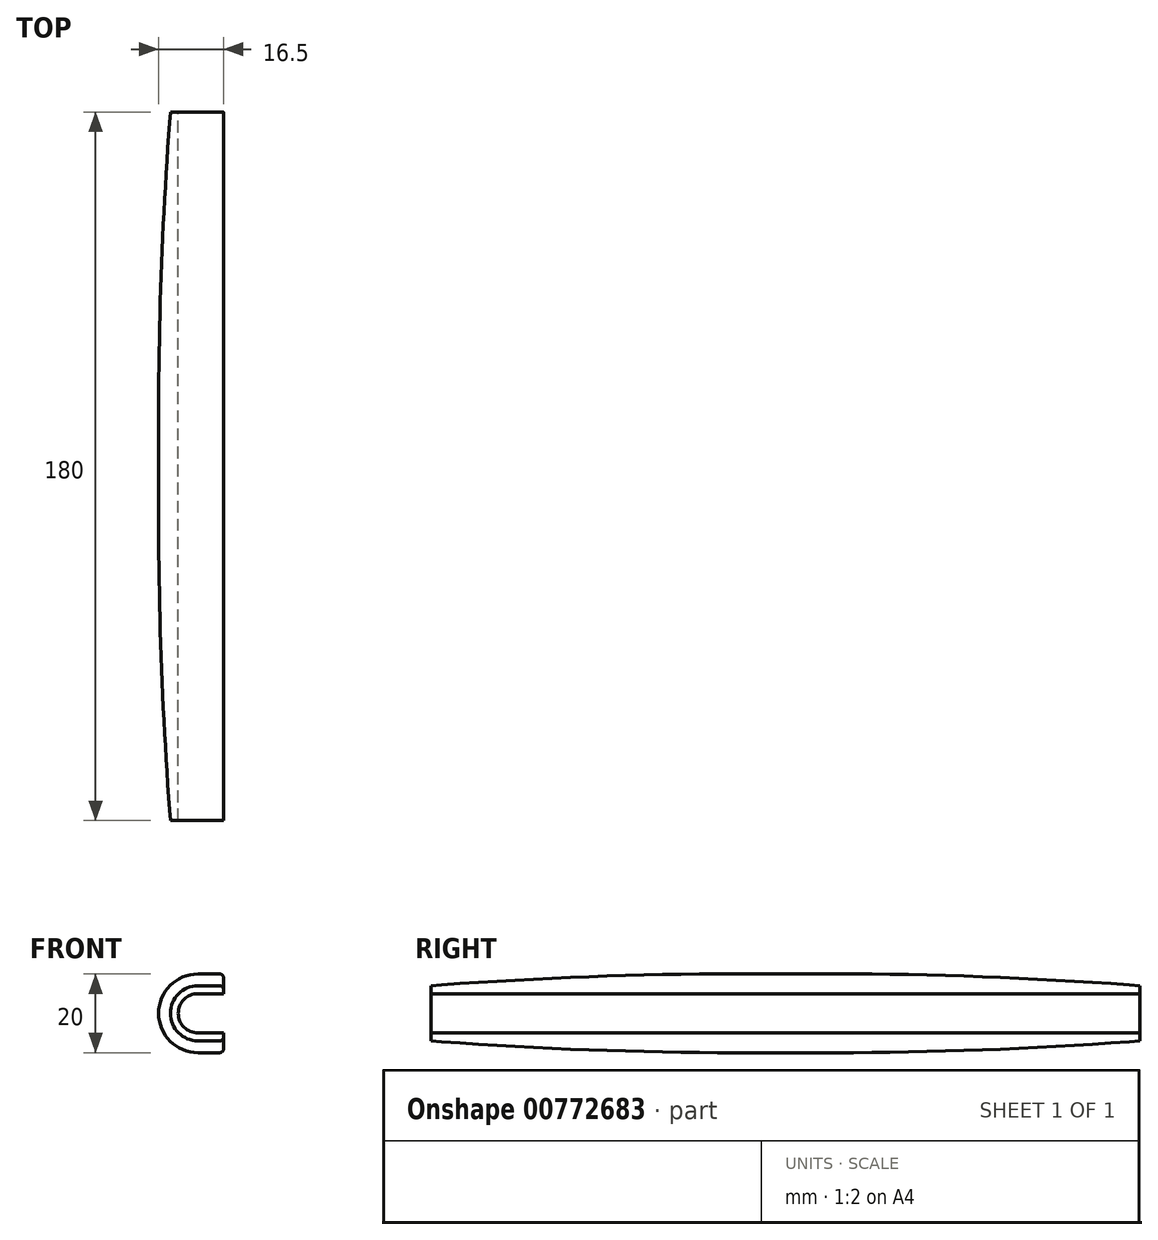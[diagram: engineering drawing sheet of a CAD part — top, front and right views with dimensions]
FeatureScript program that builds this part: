
annotation { "Feature Type Name" : "Feature", "Feature Type Description" : "" }
export const myFeature = defineFeature(function(context is Context, id is Id, definition is map)
    precondition{}
    {
        {
            var Q0;
            Q0=qCreatedBy(makeId("Front.planeOp"),FACE);
            var sketch = newSketch(context, id + "F0", { "sketchPlane" : qUnion([Q0])});
            skLineSegment(sketch, "E0.bottom", {"start": v(6.5, 5) * mm, "end": v(-6.5, 5) * mm});
            skLineSegment(sketch, "E0.top", {"start": v(6.5, -5) * mm, "end": v(-6.5, -5) * mm});
            skLineSegment(sketch, "E0.left", {"start": v(6.5, 5) * mm, "end": v(6.5, -5) * mm, "construction": true});
            skLineSegment(sketch, "E0.right", {"start": v(-6.5, 5) * mm, "end": v(-6.5, -5) * mm, "construction": true});
            skPoint(sketch, "E0.middle", {"position": v(0, 0) * mm});
            skCircle(sketch, "E1", {"center": v(-6.5, 0) * mm, "radius": 5 * mm});
            skLineSegment(sketch, "E2", {"start": v(0, 0) * mm, "end": v(0, 14.83) * mm, "construction": true});
            skCircle(sketch, "E3.MirrorC", {"center": v(6.5, 0) * mm, "radius": 5 * mm});
            skPoint(sketch, "E4", {"position": v(-11.5, 0) * mm});
            skPoint(sketch, "E5", {"position": v(11.5, 0) * mm});
            skArc(sketch, "E6", {"start": v(-6.5, 10) * mm, "mid": v(-16.5, 0) * mm, "end": v(-6.5, -10) * mm});
            skPoint(sketch, "E7", {"position": v(-16.5, 0) * mm});
            skLineSegment(sketch, "E8", {"start": v(-6.5, 10) * mm, "end": v(0, 10) * mm});
            skLineSegment(sketch, "E9", {"start": v(0, 0) * mm, "end": v(-6.5, 0) * mm, "construction": true});
            skLineSegment(sketch, "E10.MirrorCS", {"start": v(-6.5, -10) * mm, "end": v(0, -10) * mm});
            skLineSegment(sketch, "E11.MirrorCS", {"start": v(6.5, -10) * mm, "end": v(0, -10) * mm});
            skArc(sketch, "E12.MirrorC", {"start": v(-2.16, -5) * mm, "mid": v(-3.5, 0) * mm, "end": v(-2.16, 5) * mm});
            skLineSegment(sketch, "E13.MirrorCS", {"start": v(6.5, 10) * mm, "end": v(0, 10) * mm});
            skLineSegment(sketch, "E14", {"start": v(0, 10) * mm, "end": v(0, -10) * mm});
            skArc(sketch, "E15.trimOffspring", {"start": v(0, 7.6) * mm, "mid": v(16.5, 0) * mm, "end": v(0, -7.6) * mm});
            skArc(sketch, "E16.trimOffspring", {"start": v(0, -7.6) * mm, "mid": v(3.5, 0) * mm, "end": v(0, 7.6) * mm});
            skSolve(sketch);
        }
        {
            var Q0;
            Q0=makeQuery(id+"F0.imprint","IMPRINT",FACE,{"disambiguationData":[TD([[makeQuery(id+"F0.imprint","IMPRINT",EDGE,{"derivedFrom":sQuery(id+"F0.wireOp",EDGE,"E6")}),1.0]])]});
            extrude(context, id + "F1", {"entities" : qUnion([Q0]), "depth" : 180 * mm, "offsetDistance" : 25 * mm});
        }
        {
            var Q0;
            Q0=makeQuery(id+"F1.opExtrude","CAP_EDGE",EDGE,{"disambiguationData":[OSD([sQuery(id+"F0.wireOp",EDGE,"E8")])],"isStart":false});
            var Q1;
            Q1=makeQuery(id+"F1.opExtrude","CAP_EDGE",EDGE,{"disambiguationData":[OSD([sQuery(id+"F0.wireOp",EDGE,"E8")])],"isStart":true});
            chamfer(context, id + "F2", {"entities" : qUnion([Q0, Q1]), "chamferType" : ChamferType.TWO_OFFSETS, "width1" : 3 * mm, "oppositeDirection" : true, "width2" : 40 * mm, "tangentPropagation" : true});
        }
        {
            var Q0;
            {var subQ0=sQuery(id+"F0.wireOp",EDGE,"E8");Q0=makeQuery(id+"F2.opChamfer","BLEND_EDGE",EDGE,{"blendedFrom":[makeQuery(id+"F1.opExtrude","CAP_EDGE",EDGE,{"disambiguationData":[OSD([subQ0])],"isStart":false}),makeQuery(id+"F1.opExtrude","SWEPT_FACE",FACE,{"disambiguationData":[OSD([subQ0])]})],"blendedInto":[makeQuery(id+"F1.opExtrude","SWEPT_FACE",FACE,{"disambiguationData":[OSD([subQ0])]})]});}
            var Q1;
            {var subQ0=sQuery(id+"F0.wireOp",EDGE,"E8");Q1=makeQuery(id+"F2.opChamfer","BLEND_EDGE",EDGE,{"blendedFrom":[makeQuery(id+"F1.opExtrude","CAP_EDGE",EDGE,{"disambiguationData":[OSD([subQ0])],"isStart":true}),makeQuery(id+"F1.opExtrude","SWEPT_FACE",FACE,{"disambiguationData":[OSD([subQ0])]})],"blendedInto":[makeQuery(id+"F1.opExtrude","SWEPT_FACE",FACE,{"disambiguationData":[OSD([subQ0])]})]});}
            fillet(context, id + "F3", {"entities" : qUnion([Q0, Q1]), "radius" : 1000 * mm, "tangentPropagation" : true, "allowEdgeOverflow" : false});
        }
        {
            var Q0;
            Q0=makeQuery(id+"F1.opExtrude","SWEPT_EDGE",EDGE,{"disambiguationData":[OSD([sQuery(id+"F0.wireOp",EDGE,"E8"),sQuery(id+"F0.wireOp",EDGE,"E13.MirrorCS"),sQuery(id+"F0.wireOp",EDGE,"E14")])]});
            var Q1;
            Q1=makeQuery(id+"F1.opExtrude","SWEPT_EDGE",EDGE,{"disambiguationData":[OSD([sQuery(id+"F0.wireOp",EDGE,"E10.MirrorCS"),sQuery(id+"F0.wireOp",EDGE,"E11.MirrorCS"),sQuery(id+"F0.wireOp",EDGE,"E14")])]});
            fillet(context, id + "F4", {"entities" : qUnion([Q0, Q1]), "radius" : 1 * mm, "tangentPropagation" : true, "allowEdgeOverflow" : false});
        }
    });
